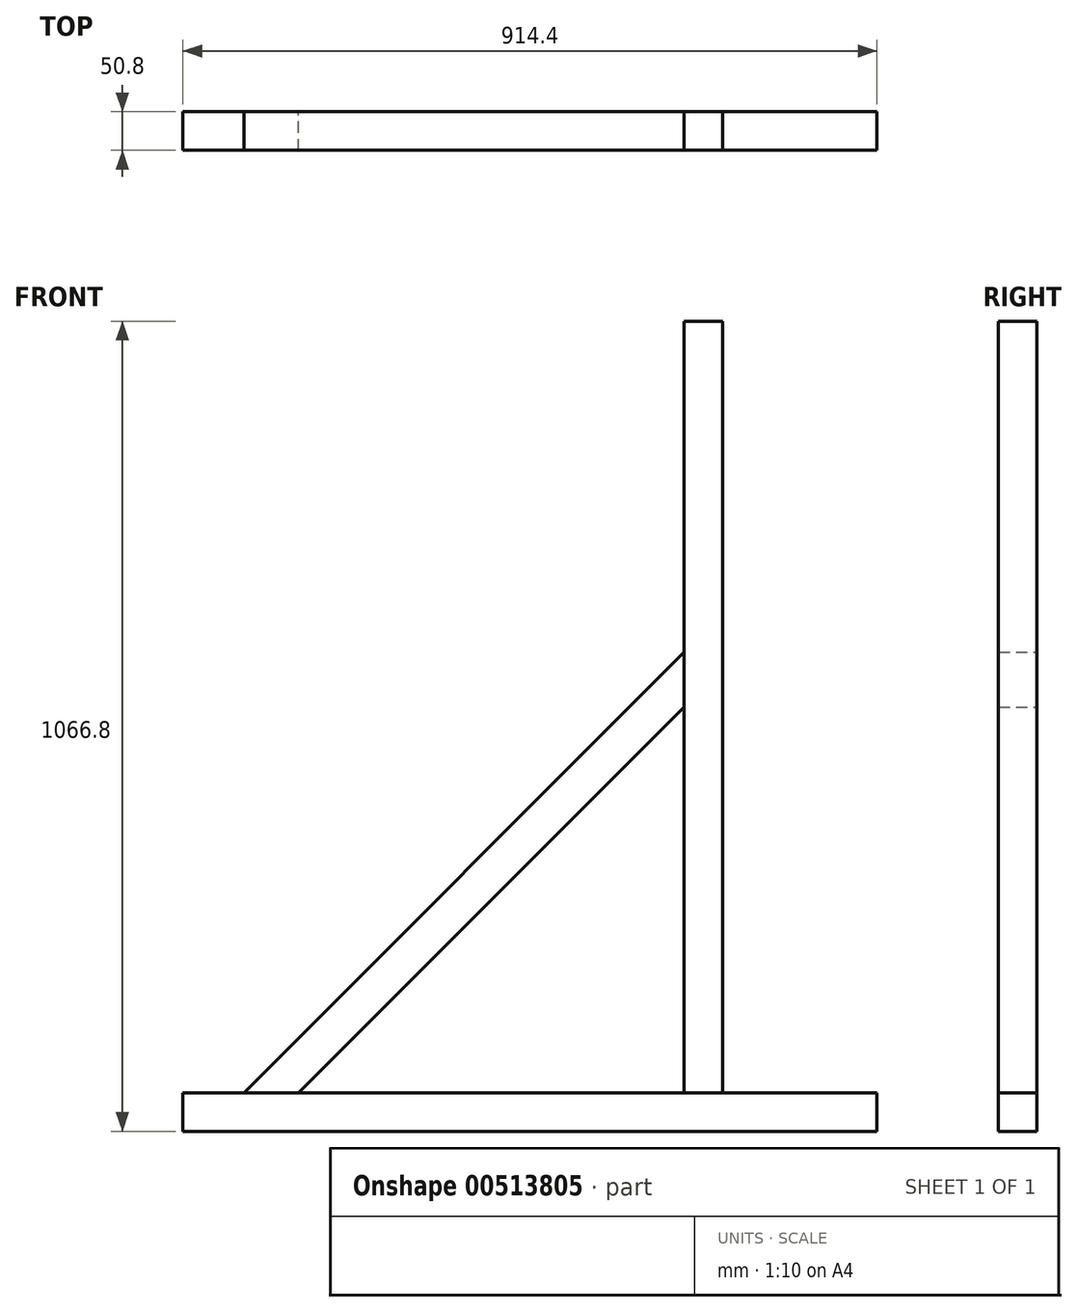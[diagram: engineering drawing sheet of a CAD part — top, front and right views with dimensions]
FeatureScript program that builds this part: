
annotation { "Feature Type Name" : "Feature", "Feature Type Description" : "" }
export const myFeature = defineFeature(function(context is Context, id is Id, definition is map)
    precondition{}
    {
        {
            var Q0;
            Q0=qCreatedBy(makeId("Front.planeOp"),FACE);
            var sketch = newSketch(context, id + "F0", { "sketchPlane" : qUnion([Q0])});
            skLineSegment(sketch, "E0.bottom", {"start": v(-147.97, -251.66) * mm, "end": v(-97.17, -251.66) * mm});
            skLineSegment(sketch, "E0.top", {"start": v(-147.97, 764.34) * mm, "end": v(-97.17, 764.34) * mm});
            skLineSegment(sketch, "E0.left", {"start": v(-147.97, -251.66) * mm, "end": v(-147.97, 764.34) * mm});
            skLineSegment(sketch, "E0.right", {"start": v(-97.17, -251.66) * mm, "end": v(-97.17, 764.34) * mm});
            skLineSegment(sketch, "E1.bottom", {"start": v(106.03, -251.66) * mm, "end": v(-808.37, -251.66) * mm});
            skLineSegment(sketch, "E1.top", {"start": v(106.03, -302.46) * mm, "end": v(-808.37, -302.46) * mm});
            skLineSegment(sketch, "E1.left", {"start": v(106.03, -251.66) * mm, "end": v(106.03, -302.46) * mm});
            skLineSegment(sketch, "E1.right", {"start": v(-808.37, -251.66) * mm, "end": v(-808.37, -302.46) * mm});
            skLineSegment(sketch, "E2", {"start": v(-147.97, 256.34) * mm, "end": v(-655.97, -251.66) * mm});
            skLineSegment(sketch, "E3.0", {"start": v(-147.97, 328.18) * mm, "end": v(-727.81, -251.66) * mm});
            skSolve(sketch);
        }
        {
            var Q0;
            {var subQ1=sQuery(id+"F0.wireOp",EDGE,"E0.top");Q0=makeQuery(id+"F0.imprint","IMPRINT",FACE,{"disambiguationData":[TD([[makeQuery(id+"F0.imprint","IMPRINT",EDGE,{"derivedFrom":subQ1}),-1.0]])]});}
            extrude(context, id + "F1", {"entities" : qUnion([Q0]), "depth" : 50.8 * mm, "offsetDistance" : 25.4 * mm, "symmetric" : true});
        }
        {
            var Q0;
            Q0=makeQuery(id+"F0.imprint","IMPRINT",FACE,{"disambiguationData":[TD([[makeQuery(id+"F0.imprint","IMPRINT",EDGE,{"derivedFrom":sQuery(id+"F0.wireOp",EDGE,"E1.top")}),-1.0]])]});
            extrude(context, id + "F2", {"entities" : qUnion([Q0]), "depth" : 50.8 * mm, "offsetDistance" : 25.4 * mm, "symmetric" : true});
        }
        {
            var Q0;
            {var subQ0=sQuery(id+"F0.wireOp",EDGE,"E2");Q0=makeQuery(id+"F0.imprint","IMPRINT",FACE,{"disambiguationData":[TD([[makeQuery(id+"F0.imprint","IMPRINT",EDGE,{"derivedFrom":subQ0}),-1.0]])]});}
            extrude(context, id + "F3", {"entities" : qUnion([Q0]), "depth" : 50.8 * mm, "offsetDistance" : 25.4 * mm, "symmetric" : true});
        }
    });
